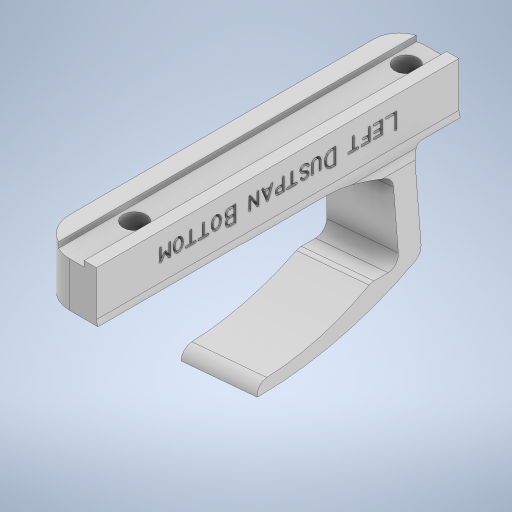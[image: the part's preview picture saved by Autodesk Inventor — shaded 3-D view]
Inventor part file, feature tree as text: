
AUTODESK INVENTOR PART (.ipt)
format: ipt  version: 2024 (Build 280153000, 153)  size: 773,120 bytes
history: native  units: mm
features: extrude x8, sketch x7, fillet x2, plane x1, projected_geometry x1
ambient origin geometry x8: Origin, YZ Plane, XZ Plane, XY Plane, X Axis, Y Axis, Z Axis, Center Point
bodies: Solid1 (feature_tree)
feature tree (19):
  sketch  "Sketch1"  dims[d0=4.1mm d1=3.2mm]
  extrude  "Extrusion1"  Depth=3.2mm
  extrude  "Extrusion2"  Depth=48.5mm
  extrude  "Extrusion3"  Depth=1.0mm
  sketch  "Sketch3"  dims[d2=7.3mm d3=48.5mm]
  plane  "Work Plane1"
  extrude  "Extrusion8"  Depth=10.0mm
  extrude  "Extrusion9"  Depth=8.0mm TaperAngle=0.0deg
  extrude  "Extrusion10"  Depth=0.872665mm
  fillet  "Fillet1"  Radius=30.0mm
  extrude  "Extrusion11"  Depth=15.5mm TaperAngle=0.0deg
  fillet  "Fillet3"  Radius=2.4mm
  extrude  "Extrusion12"  Depth=5.0mm
  sketch  "Sketch8"  dims[d5=3.0mm d6=1.0mm]
  sketch  "Sketch9"  dims[d7=3.2mm d8=10.0mm]
  sketch  "Sketch10"  dims[d9=1.0mm d10=0.0mm d11=8.0mm d12=0.0mm]
  sketch  "Sketch11"  dims[d13=5.0mm d14=0.0mm d30=0.872665mm d31=30.0mm d32=0.0mm]
  sketch  "Sketch12"  dims[d33=11.0mm d34=15.5mm d35=0.0mm d36=2.4mm d37=5.0mm d38=5.0mm d39=2.0mm d40=10.9mm d41=0.0mm d42=2.0mm d44=1.0mm d45=0.0mm d46=2.0mm d47=1.0mm d48=0.0mm]
  projected_geometry  "Projected Loop3"
